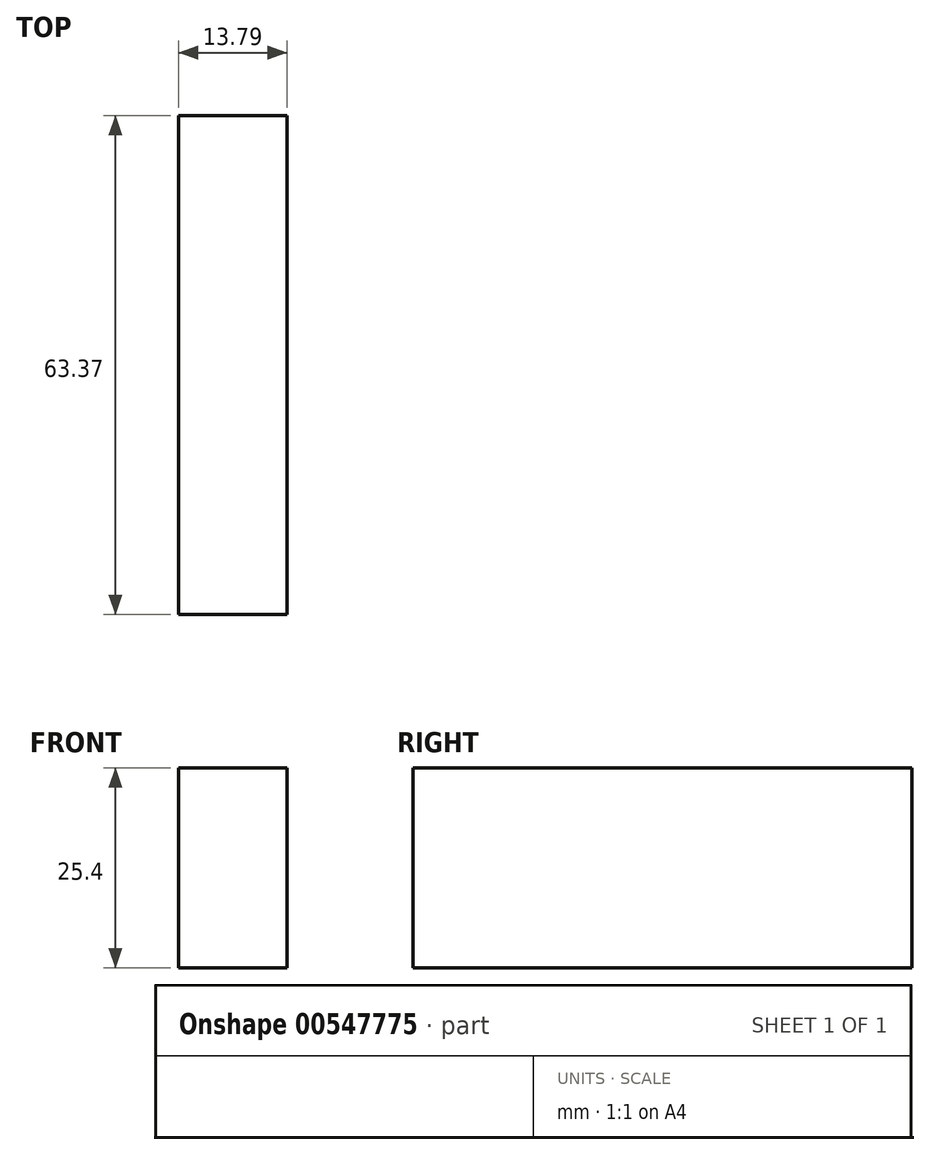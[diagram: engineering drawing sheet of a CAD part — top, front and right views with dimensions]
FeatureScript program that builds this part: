
annotation { "Feature Type Name" : "Feature", "Feature Type Description" : "" }
export const myFeature = defineFeature(function(context is Context, id is Id, definition is map)
    precondition{}
    {
        {
            var Q0;
            Q0=qCreatedBy(makeId("Top.planeOp"),FACE);
            var sketch = newSketch(context, id + "F0", { "sketchPlane" : qUnion([Q0])});
            skLineSegment(sketch, "E0.bottom", {"start": v(-49.38, -41.79) * mm, "end": v(-35.59, -41.79) * mm});
            skLineSegment(sketch, "E0.top", {"start": v(-49.38, 21.58) * mm, "end": v(-35.59, 21.58) * mm});
            skLineSegment(sketch, "E0.left", {"start": v(-49.38, -41.79) * mm, "end": v(-49.38, 21.58) * mm});
            skLineSegment(sketch, "E0.right", {"start": v(-35.59, -41.79) * mm, "end": v(-35.59, 21.58) * mm});
            skSolve(sketch);
        }
        {
            var Q0;
            Q0 = qSketchRegion(id + "F0", true);
            extrude(context, id + "F1", {"entities" : qUnion([Q0]), "depth" : 25.4 * mm, "offsetDistance" : 25.4 * mm});
        }
    });
